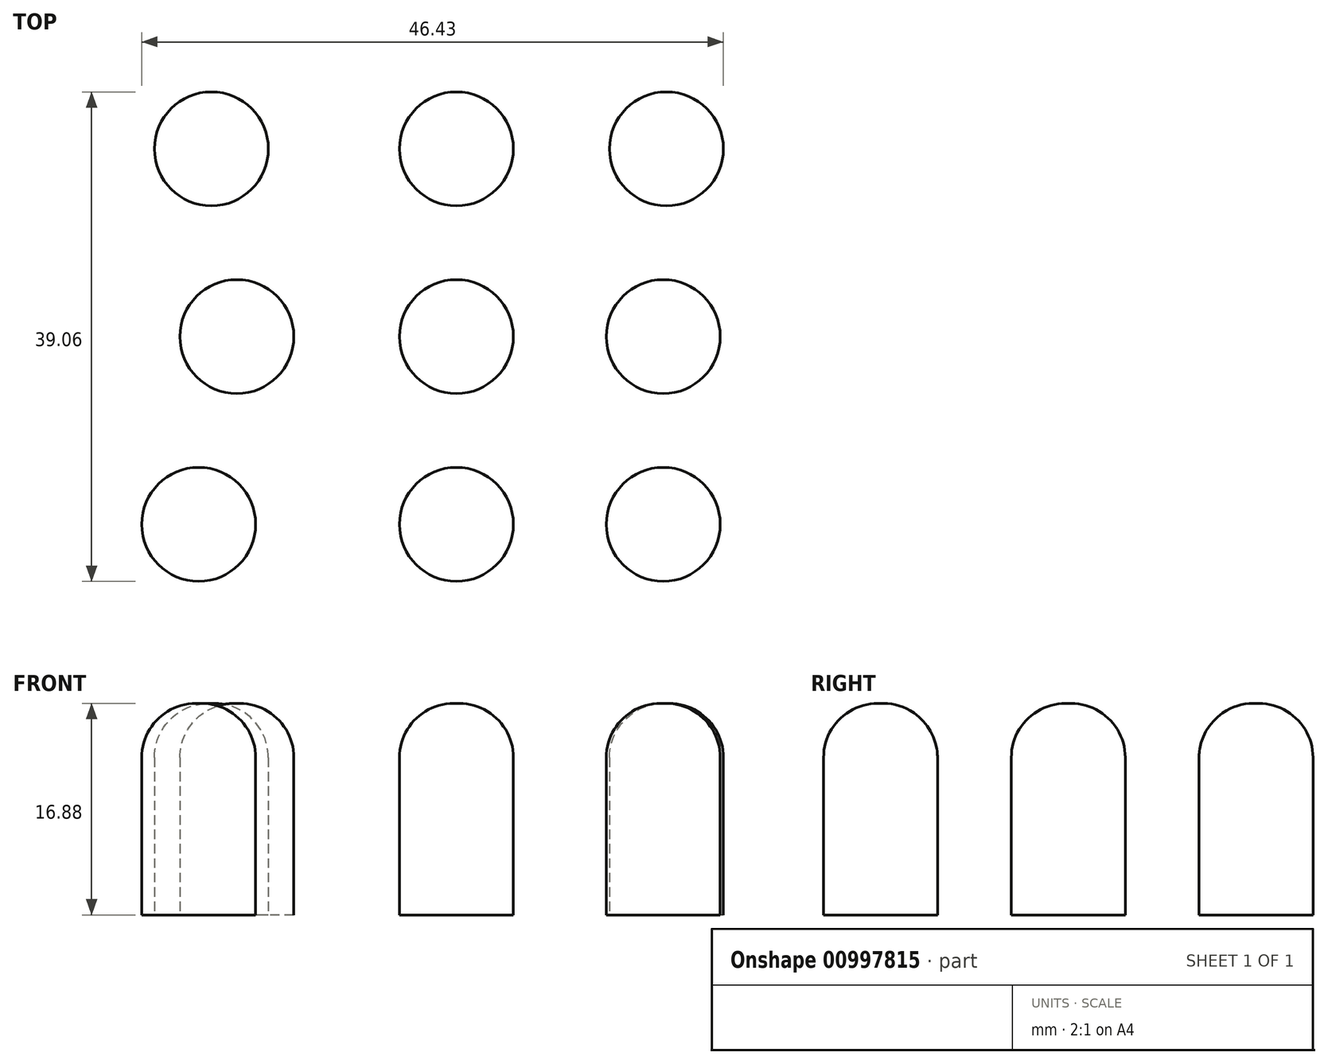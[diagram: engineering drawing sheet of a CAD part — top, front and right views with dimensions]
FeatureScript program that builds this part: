
annotation { "Feature Type Name" : "Feature", "Feature Type Description" : "" }
export const myFeature = defineFeature(function(context is Context, id is Id, definition is map)
    precondition{}
    {
        {
            var Q0;
            Q0=qCreatedBy(makeId("Top.planeOp"),FACE);
            var sketch = newSketch(context, id + "F0", { "sketchPlane" : qUnion([Q0])});
            skCircle(sketch, "E0", {"center": v(0, 0) * mm, "radius": 4.55 * mm});
            skSolve(sketch);
        }
        {
            var Q0;
            Q0=makeQuery(id+"F0.imprint","IMPRINT",FACE,{"disambiguationData":[TD([[makeQuery(id+"F0.imprint","IMPRINT",EDGE,{"derivedFrom":sQuery(id+"F0.wireOp",EDGE,"E0")}),1.0]])]});
            extrude(context, id + "F1", {"entities" : qUnion([Q0]), "depth" : 16.88 * mm, "offsetDistance" : 25.4 * mm});
        }
        {
            var Q0;
            Q0=makeQuery(id+"F1.opExtrude","CAP_EDGE",EDGE,{"disambiguationData":[OSD([sQuery(id+"F0.wireOp",EDGE,"E0")])],"isStart":false});
            fillet(context, id + "F2", {"entities" : qUnion([Q0]), "radius" : 4.32 * mm, "tangentPropagation" : true, "allowEdgeOverflow" : false});
        }
        {
            var Q0;
            Q0=makeQuery(id+"F1.opExtrude","SWEPT_BODY",BODY,{"disambiguationData":[OSD([sQuery(id+"F0.wireOp",EDGE,"E0")])]});
            transform(context, id + "F3", {"entities" : qUnion([Q0]), "transformType" : TransformType.TRANSLATION_3D, "dx" : 0 * mm, "dy" : 15 * mm, "dz" : 0 * mm, "makeCopy" : true});
        }
        {
            var Q0;
            Q0=makeQuery(id+"F1.opExtrude","SWEPT_BODY",BODY,{"disambiguationData":[OSD([sQuery(id+"F0.wireOp",EDGE,"E0")])]});
            transform(context, id + "F4", {"entities" : qUnion([Q0]), "transformType" : TransformType.TRANSLATION_3D, "dx" : 0 * mm, "dy" : -15 * mm, "dz" : 0 * mm, "makeCopy" : true});
        }
        {
            var Q0;
            Q0=makeQuery(id+"F3.opPattern","COPY",BODY,{"derivedFrom":makeQuery(id+"F1.opExtrude","SWEPT_BODY",BODY,{"disambiguationData":[OSD([sQuery(id+"F0.wireOp",EDGE,"E0")])]}),"instanceName":"1"});
            transform(context, id + "F5", {"entities" : qUnion([Q0]), "transformType" : TransformType.TRANSLATION_3D, "dx" : 16.76 * mm, "dy" : 0 * mm, "dz" : 0 * mm, "makeCopy" : true});
        }
        {
            var Q0;
            Q0=makeQuery(id+"F3.opPattern","COPY",BODY,{"derivedFrom":makeQuery(id+"F1.opExtrude","SWEPT_BODY",BODY,{"disambiguationData":[OSD([sQuery(id+"F0.wireOp",EDGE,"E0")])]}),"instanceName":"1"});
            transform(context, id + "F6", {"entities" : qUnion([Q0]), "transformType" : TransformType.TRANSLATION_3D, "dx" : -19.56 * mm, "dy" : 0 * mm, "dz" : 0 * mm, "makeCopy" : true});
        }
        {
            var Q0;
            Q0=makeQuery(id+"F1.opExtrude","SWEPT_BODY",BODY,{"disambiguationData":[OSD([sQuery(id+"F0.wireOp",EDGE,"E0")])]});
            transform(context, id + "F7", {"entities" : qUnion([Q0]), "transformType" : TransformType.TRANSLATION_3D, "dx" : 16.5 * mm, "dy" : 0 * mm, "dz" : 0 * mm, "makeCopy" : true});
        }
        {
            var Q0;
            Q0=makeQuery(id+"F1.opExtrude","SWEPT_BODY",BODY,{"disambiguationData":[OSD([sQuery(id+"F0.wireOp",EDGE,"E0")])]});
            transform(context, id + "F8", {"entities" : qUnion([Q0]), "transformType" : TransformType.TRANSLATION_3D, "dx" : -17.53 * mm, "dy" : 0 * mm, "dz" : 0 * mm, "makeCopy" : true});
        }
        {
            var Q0;
            Q0=makeQuery(id+"F4.opPattern","COPY",BODY,{"derivedFrom":makeQuery(id+"F1.opExtrude","SWEPT_BODY",BODY,{"disambiguationData":[OSD([sQuery(id+"F0.wireOp",EDGE,"E0")])]}),"instanceName":"1"});
            transform(context, id + "F9", {"entities" : qUnion([Q0]), "transformType" : TransformType.TRANSLATION_3D, "dx" : 16.5 * mm, "dy" : 0 * mm, "dz" : 0 * mm, "makeCopy" : true});
        }
        {
            var Q0;
            Q0=makeQuery(id+"F4.opPattern","COPY",BODY,{"derivedFrom":makeQuery(id+"F1.opExtrude","SWEPT_BODY",BODY,{"disambiguationData":[OSD([sQuery(id+"F0.wireOp",EDGE,"E0")])]}),"instanceName":"1"});
            transform(context, id + "F10", {"entities" : qUnion([Q0]), "transformType" : TransformType.TRANSLATION_3D, "dx" : -20.57 * mm, "dy" : 0 * mm, "dz" : 0 * mm, "makeCopy" : true});
        }
    });
